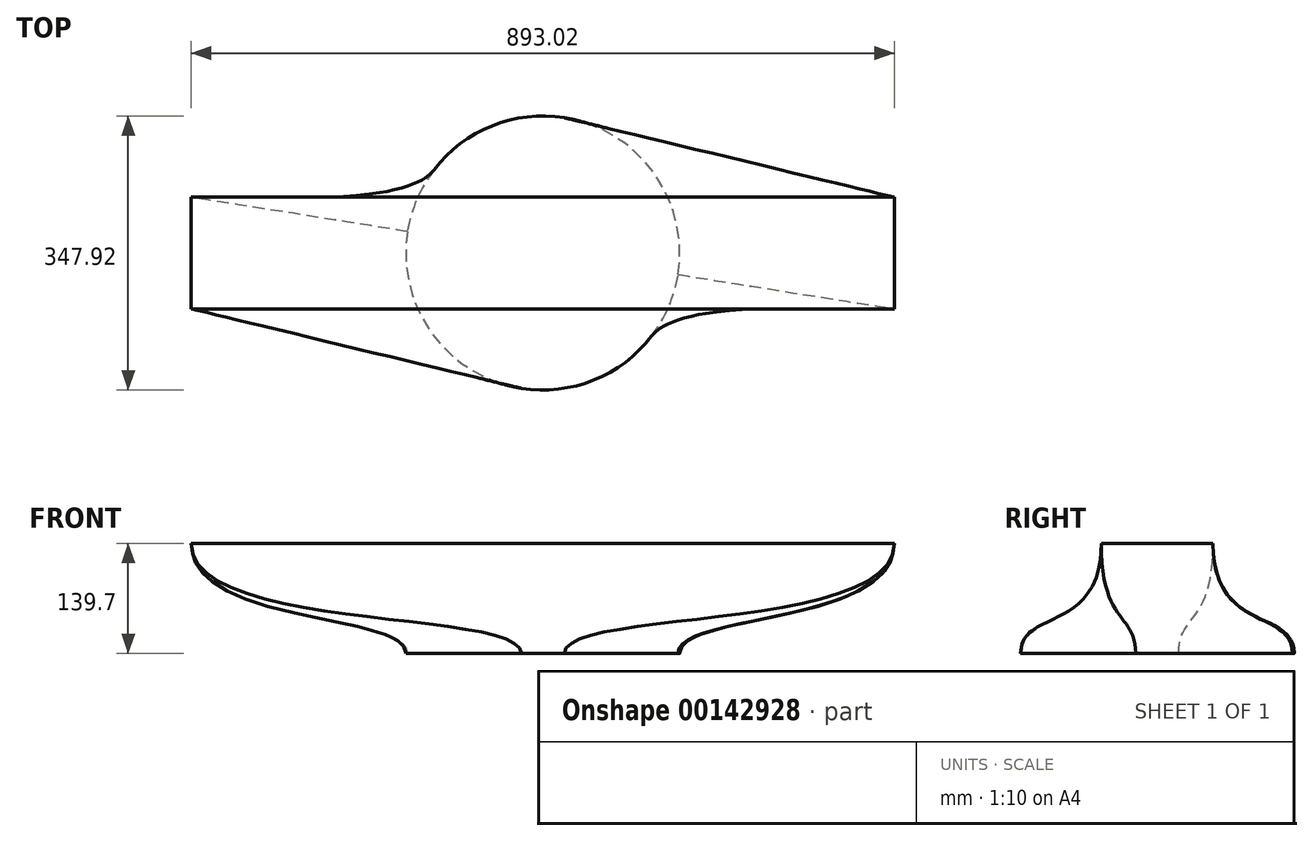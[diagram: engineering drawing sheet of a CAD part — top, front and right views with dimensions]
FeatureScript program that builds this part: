
annotation { "Feature Type Name" : "Feature", "Feature Type Description" : "" }
export const myFeature = defineFeature(function(context is Context, id is Id, definition is map)
    precondition{}
    {
        {
            var Q0;
            Q0=qCreatedBy(makeId("Top.planeOp"),FACE);
            var sketch = newSketch(context, id + "F0", { "sketchPlane" : qUnion([Q0])});
            skCircle(sketch, "E0", {"center": v(0, 0) * mm, "radius": 173.96 * mm});
            skSolve(sketch);
        }
        {
            var Q0;
            Q0=makeQuery(id+"F0.imprint","IMPRINT",FACE,{"disambiguationData":[TD([[makeQuery(id+"F0.imprint","IMPRINT",EDGE,{"derivedFrom":sQuery(id+"F0.wireOp",EDGE,"E0")}),1.0]])]});
            cPlane(context, id + "F1", {"entities" : qUnion([Q0]), "cplaneType" : CPlaneType.OFFSET, "offset" : 139.7 * mm, "width" : 152.4 * mm, "height" : 152.4 * mm});
        }
        {
            var Q0;
            Q0=qCreatedBy(id+"F1.planeOp",FACE);
            var sketch = newSketch(context, id + "F2", { "sketchPlane" : qUnion([Q0])});
            skLineSegment(sketch, "E1.bottom", {"start": v(446.5, -70.9) * mm, "end": v(-446.5, -70.9) * mm});
            skLineSegment(sketch, "E1.top", {"start": v(446.5, 70.9) * mm, "end": v(-446.5, 70.9) * mm});
            skLineSegment(sketch, "E1.left", {"start": v(446.5, -70.9) * mm, "end": v(446.5, 70.9) * mm});
            skLineSegment(sketch, "E1.right", {"start": v(-446.5, -70.9) * mm, "end": v(-446.5, 70.9) * mm});
            skPoint(sketch, "E1.middle", {"position": v(0, 0) * mm});
            skSolve(sketch);
        }
        {
            var Q0;
            Q0=makeQuery(id+"F0.imprint","IMPRINT",FACE,{"disambiguationData":[TD([[makeQuery(id+"F0.imprint","IMPRINT",EDGE,{"derivedFrom":sQuery(id+"F0.wireOp",EDGE,"E0")}),1.0]])]});
            var Q1;
            Q1=makeQuery(id+"F2.imprint","IMPRINT",FACE,{"disambiguationData":[TD([[makeQuery(id+"F2.imprint","IMPRINT",EDGE,{"derivedFrom":sQuery(id+"F2.wireOp",EDGE,"E1.bottom")}),-1.0]])]});
            loft(context, id + "F3", {"startCondition" : LoftEndDerivativeType.NORMAL_TO_PROFILE, "startMagnitude" : 1, "endCondition" : LoftEndDerivativeType.NORMAL_TO_PROFILE, "endMagnitude" : 2, "sheetProfilesArray" : [{ "sheetProfileEntities" : qUnion([Q0]) }, { "sheetProfileEntities" : qUnion([Q1]) }]});
        }
    });
